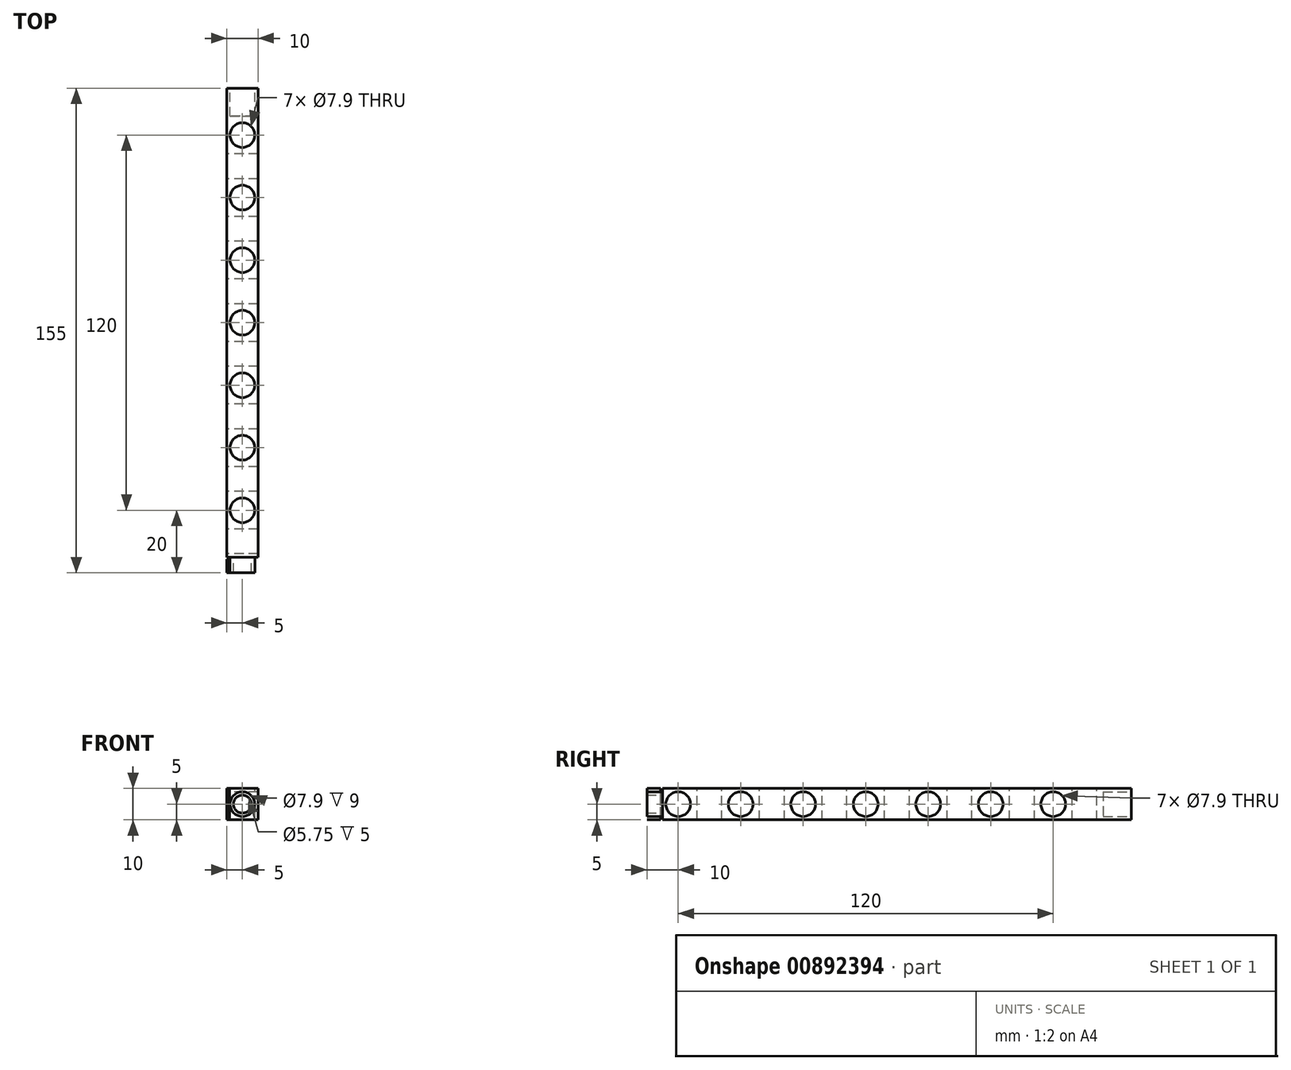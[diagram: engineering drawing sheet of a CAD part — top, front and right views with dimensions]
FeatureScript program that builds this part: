
annotation { "Feature Type Name" : "Feature", "Feature Type Description" : "" }
export const myFeature = defineFeature(function(context is Context, id is Id, definition is map)
    precondition{}
    {
        {
            var Q0;
            Q0=qCreatedBy(makeId("Top.planeOp"),FACE);
            var sketch = newSketch(context, id + "F0", { "sketchPlane" : qUnion([Q0])});
            skLineSegment(sketch, "E0.bottom", {"start": v(-5, -75) * mm, "end": v(5, -75) * mm});
            skLineSegment(sketch, "E0.top", {"start": v(-5, 75) * mm, "end": v(5, 75) * mm});
            skLineSegment(sketch, "E0.left", {"start": v(-5, -75) * mm, "end": v(-5, 75) * mm});
            skLineSegment(sketch, "E0.right", {"start": v(5, -75) * mm, "end": v(5, 75) * mm});
            skSolve(sketch);
        }
        {
            var Q0;
            Q0 = qSketchRegion(id + "F0", true);
            extrude(context, id + "F1", {"entities" : qUnion([Q0]), "depth" : 10 * mm, "offsetDistance" : 25 * mm});
        }
        {
            var Q0;
            Q0=makeQuery(id+"F1.opExtrude","CAP_FACE",FACE,{"disambiguationData":[OSD([sQuery(id+"F0.wireOp",EDGE,"E0.bottom"),sQuery(id+"F0.wireOp",EDGE,"E0.top"),sQuery(id+"F0.wireOp",EDGE,"E0.left"),sQuery(id+"F0.wireOp",EDGE,"E0.right")])],"isStart":false});
            var sketch = newSketch(context, id + "F2", { "sketchPlane" : qUnion([Q0])});
            skCircle(sketch, "E1", {"center": v(0, 0) * mm, "radius": 3.95 * mm});
            skCircle(sketch, "E2", {"center": v(0, 20) * mm, "radius": 3.95 * mm});
            skCircle(sketch, "E3", {"center": v(0, 40) * mm, "radius": 3.95 * mm});
            skCircle(sketch, "E4", {"center": v(0, 60) * mm, "radius": 3.95 * mm});
            skCircle(sketch, "E5", {"center": v(0, -20) * mm, "radius": 3.95 * mm});
            skCircle(sketch, "E6", {"center": v(0, -40) * mm, "radius": 3.95 * mm});
            skCircle(sketch, "E7", {"center": v(0, -60) * mm, "radius": 3.95 * mm});
            skSolve(sketch);
        }
        {
            var Q0;
            Q0 = qSketchRegion(id + "F2", true);
            extrude(context, id + "F3", {"entities" : qUnion([Q0]), "operationType" : NewBodyOperationType.REMOVE, "oppositeDirection" : true, "depth" : 25 * mm, "offsetDistance" : 25 * mm});
        }
        {
            var Q0;
            Q0=makeQuery(id+"F1.opExtrude","SWEPT_FACE",FACE,{"disambiguationData":[OSD([sQuery(id+"F0.wireOp",EDGE,"E0.left")])]});
            var sketch = newSketch(context, id + "F4", { "sketchPlane" : qUnion([Q0])});
            skCircle(sketch, "E8", {"center": v(-10, 5) * mm, "radius": 3.95 * mm});
            skCircle(sketch, "E9", {"center": v(-30, 5) * mm, "radius": 3.95 * mm});
            skCircle(sketch, "E10", {"center": v(-50, 5) * mm, "radius": 3.95 * mm});
            skCircle(sketch, "E11", {"center": v(10, 5) * mm, "radius": 3.95 * mm});
            skCircle(sketch, "E12", {"center": v(30, 5) * mm, "radius": 3.95 * mm});
            skCircle(sketch, "E13", {"center": v(50, 5) * mm, "radius": 3.95 * mm});
            skCircle(sketch, "E14", {"center": v(70, 5) * mm, "radius": 3.95 * mm});
            skSolve(sketch);
        }
        {
            var Q0;
            Q0 = qSketchRegion(id + "F4", true);
            extrude(context, id + "F5", {"entities" : qUnion([Q0]), "operationType" : NewBodyOperationType.REMOVE, "oppositeDirection" : true, "depth" : 25 * mm, "offsetDistance" : 25 * mm});
        }
        {
            var Q0;
            Q0=makeQuery(id+"F1.opExtrude","SWEPT_FACE",FACE,{"disambiguationData":[OSD([sQuery(id+"F0.wireOp",EDGE,"E0.top")])]});
            var sketch = newSketch(context, id + "F6", { "sketchPlane" : qUnion([Q0])});
            skCircle(sketch, "E15", {"center": v(0, 5) * mm, "radius": 3.95 * mm});
            skPoint(sketch, "E15.centerSnap0", {"position": v(0, 10) * mm});
            skSolve(sketch);
        }
        {
            var Q0;
            Q0 = qSketchRegion(id + "F6", true);
            extrude(context, id + "F7", {"entities" : qUnion([Q0]), "operationType" : NewBodyOperationType.REMOVE, "oppositeDirection" : true, "depth" : 9 * mm, "offsetDistance" : 25 * mm});
        }
        {
            var Q0;
            Q0=makeQuery(id+"F1.opExtrude","SWEPT_FACE",FACE,{"disambiguationData":[OSD([sQuery(id+"F0.wireOp",EDGE,"E0.bottom")])]});
            var sketch = newSketch(context, id + "F8", { "sketchPlane" : qUnion([Q0])});
            skCircle(sketch, "E16", {"center": v(0, 5) * mm, "radius": 3.95 * mm});
            skPoint(sketch, "E16.centerSnap0", {"position": v(5, 5) * mm});
            skCircle(sketch, "E17", {"center": v(0, 5) * mm, "radius": 2.87 * mm});
            skSolve(sketch);
        }
        {
            var Q0;
            Q0 = qSketchRegion(id + "F8", true);
            extrude(context, id + "F9", {"entities" : qUnion([Q0]), "operationType" : NewBodyOperationType.ADD, "depth" : 5 * mm, "offsetDistance" : 25 * mm});
        }
        {
            var Q0;
            {var subQ1=sQuery(id+"F0.wireOp",EDGE,"E0.left");var subQ3=sQuery(id+"F0.wireOp",EDGE,"E0.bottom");Q0=makeQuery(id+"F9.boolean.opBoolean","SPLIT",FACE,{"disambiguationData":[TD([makeQuery(id+"F1.opExtrude","SWEPT_FACE",FACE,{"disambiguationData":[OSD([subQ1])]})])],"derivedFrom":makeQuery(id+"F1.opExtrude","SWEPT_FACE",FACE,{"disambiguationData":[OSD([subQ3])]})});}
            var sketch = newSketch(context, id + "F10", { "sketchPlane" : qUnion([Q0])});
            skLineSegment(sketch, "E18.bottom", {"start": v(-5, 10) * mm, "end": v(-4.15, 10) * mm});
            skLineSegment(sketch, "E18.top", {"start": v(-5, 0) * mm, "end": v(-4.15, 0) * mm});
            skLineSegment(sketch, "E18.left", {"start": v(-5, 10) * mm, "end": v(-5, 0) * mm});
            skLineSegment(sketch, "E18.right", {"start": v(-4.15, 10) * mm, "end": v(-4.15, 0) * mm});
            skSolve(sketch);
        }
        {
            var Q0;
            Q0 = qSketchRegion(id + "F10", true);
            extrude(context, id + "F11", {"entities" : qUnion([Q0]), "operationType" : NewBodyOperationType.ADD, "depth" : 5 * mm, "offsetDistance" : 25 * mm});
        }
        {
            var Q0;
            Q0=makeQuery(id+"F11.boolean.opBoolean","MERGE",FACE,{"derivedFrom":[makeQuery(id+"F1.opExtrude","CAP_FACE",FACE,{"disambiguationData":[OSD([sQuery(id+"F0.wireOp",EDGE,"E0.bottom"),sQuery(id+"F0.wireOp",EDGE,"E0.top"),sQuery(id+"F0.wireOp",EDGE,"E0.left"),sQuery(id+"F0.wireOp",EDGE,"E0.right")])],"isStart":false}),makeQuery(id+"F11.opExtrude","SWEPT_FACE",FACE,{"disambiguationData":[OSD([sQuery(id+"F10.wireOp",EDGE,"E18.bottom")])]})]});
            var sketch = newSketch(context, id + "F12", { "sketchPlane" : qUnion([Q0])});
            skLineSegment(sketch, "E19.bottom", {"start": v(-6.44, -75) * mm, "end": v(-4.15, -75) * mm});
            skLineSegment(sketch, "E19.top", {"start": v(-6.44, -75.66) * mm, "end": v(-4.15, -75.66) * mm});
            skLineSegment(sketch, "E19.left", {"start": v(-6.44, -75) * mm, "end": v(-6.44, -75.66) * mm});
            skLineSegment(sketch, "E19.right", {"start": v(-4.15, -75) * mm, "end": v(-4.15, -75.66) * mm});
            skSolve(sketch);
        }
        {
            var Q0;
            Q0 = qSketchRegion(id + "F12", true);
            extrude(context, id + "F13", {"entities" : qUnion([Q0]), "operationType" : NewBodyOperationType.REMOVE, "oppositeDirection" : true, "depth" : 25 * mm, "offsetDistance" : 25 * mm});
        }
    });
